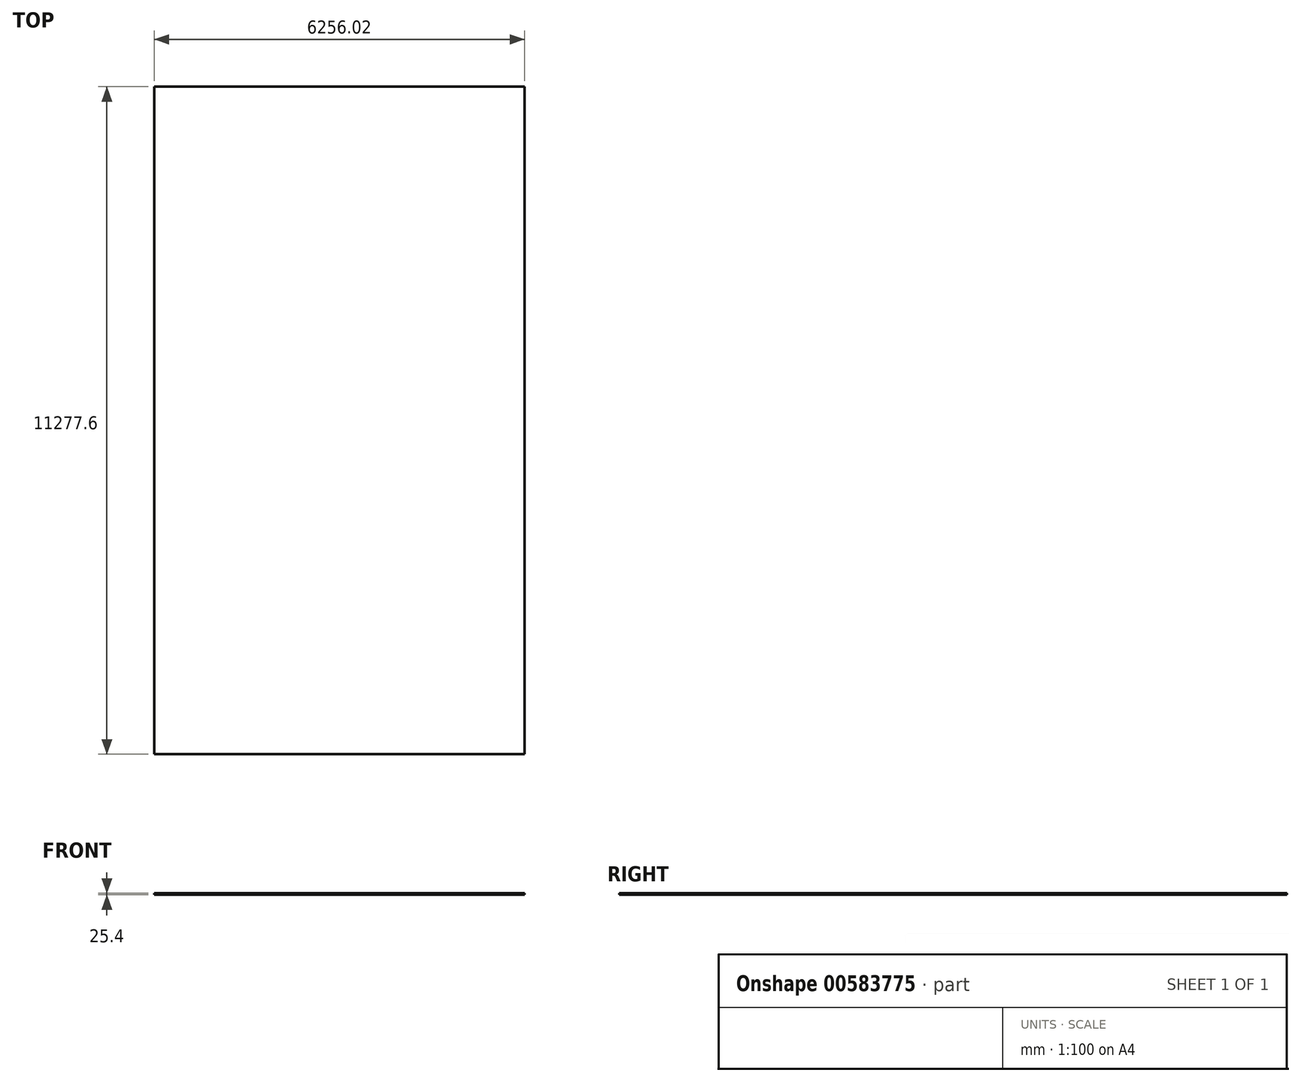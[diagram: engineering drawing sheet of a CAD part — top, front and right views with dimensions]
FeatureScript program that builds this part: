
annotation { "Feature Type Name" : "Feature", "Feature Type Description" : "" }
export const myFeature = defineFeature(function(context is Context, id is Id, definition is map)
    precondition{}
    {
        {
            var Q0;
            Q0=qCreatedBy(makeId("Top.planeOp"),FACE);
            var sketch = newSketch(context, id + "F0", { "sketchPlane" : qUnion([Q0])});
            skLineSegment(sketch, "E0.bottom", {"start": v(0, -1146.15) * mm, "end": v(6256.02, -1146.15) * mm});
            skLineSegment(sketch, "E0.top", {"start": v(0, 10131.45) * mm, "end": v(6256.02, 10131.45) * mm});
            skLineSegment(sketch, "E0.left", {"start": v(0, -1146.15) * mm, "end": v(0, 10131.45) * mm});
            skLineSegment(sketch, "E0.right", {"start": v(6256.02, -1146.15) * mm, "end": v(6256.02, 10131.45) * mm});
            skSolve(sketch);
        }
        {
            var Q0;
            Q0=makeQuery(id+"F0.imprint","IMPRINT",FACE,{"disambiguationData":[TD([[makeQuery(id+"F0.imprint","IMPRINT",EDGE,{"derivedFrom":sQuery(id+"F0.wireOp",EDGE,"E0.bottom")}),1.0]])]});
            extrude(context, id + "F1", {"entities" : qUnion([Q0]), "depth" : 25.4 * mm, "offsetDistance" : 25.4 * mm});
        }
    });
